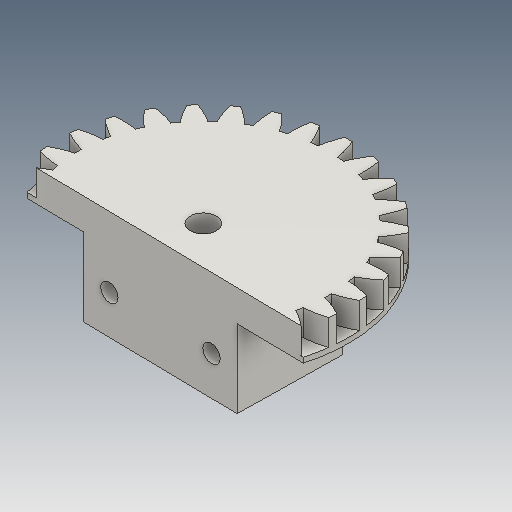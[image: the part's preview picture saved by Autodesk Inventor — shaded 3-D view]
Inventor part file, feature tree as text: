
AUTODESK INVENTOR PART (.ipt)
format: ipt  version: 2018 (Build 220112000, 112)  size: 298,496 bytes
history: native  units: mm
features: other x13, sketch x9, plane x4
ambient origin geometry x8: Origin, YZ Plane, XZ Plane, XY Plane, X Axis, Y Axis, Z Axis, Center Point
bodies: Volumenkörper1 (feature_tree)
feature tree (26):
  other  "Stirnzahnrad1"
  other  "Solid1::Stirnzahnrad1"
  other  "Bezeichnung1"
  sketch  "Sketch1"  dims[d0=10.0mm]
  sketch  "Sketch2"  dims[d16=40.0mm]
  sketch  "Skizze9"  dims[d17=0.0mm]
  sketch  "Skizze10"  dims[d41=0.0mm]
  sketch  "Skizze11"  dims[d43=40.0mm]
  sketch  "Skizze12"  dims[d46=40.0mm]
  sketch  "Skizze13"  dims[d47=0.0mm]
  sketch  "Skizze14"  dims[d48=0.0mm]
  sketch  "Skizze15"
  plane  "XZ Plane_1"
  plane  "Work Plane2"
  plane  "Work Plane8"
  plane  "Work Plane9"
  other  "Z Axis_1"
  other  "Flä1"
  other  "Srf1::Abgeleitet"
  other  "Abstands-iMate"
  other  "Ausrichtungs-iMate"
  other  "Netz-iMate"
  other  "Achsen-iMate"
  other  "Positions-iMate"
  other  "Netz-iMate 2"
  other  "Startebenen-iMate"
